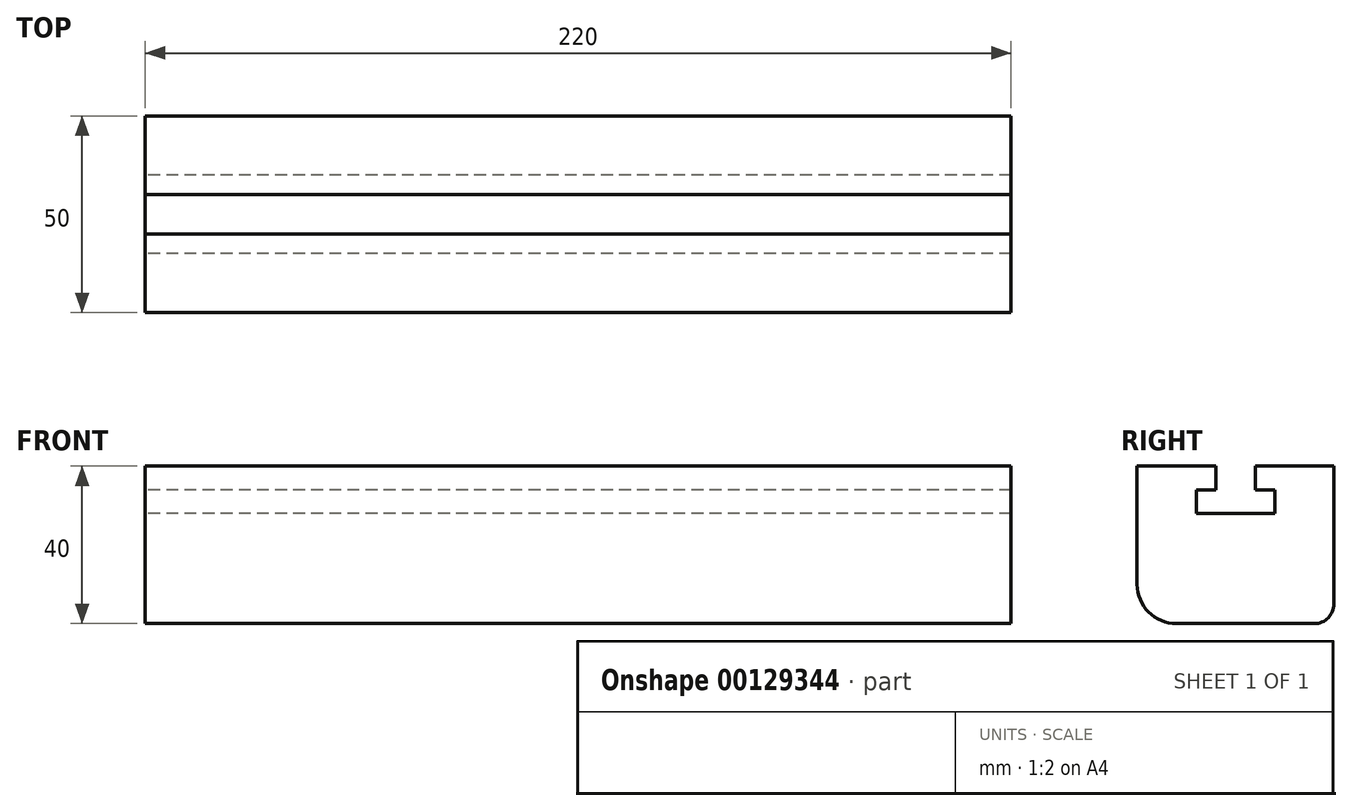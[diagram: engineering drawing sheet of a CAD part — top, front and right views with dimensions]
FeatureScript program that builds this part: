
annotation { "Feature Type Name" : "Feature", "Feature Type Description" : "" }
export const myFeature = defineFeature(function(context is Context, id is Id, definition is map)
    precondition{}
    {
        {
            var Q0;
            Q0=qCreatedBy(makeId("Right.planeOp"),FACE);
            var sketch = newSketch(context, id + "F0", { "sketchPlane" : qUnion([Q0])});
            skLineSegment(sketch, "E0.bottom", {"start": v(50, 40) * mm, "end": v(30, 40) * mm});
            skLineSegment(sketch, "E0.top", {"start": v(45, 0) * mm, "end": v(0, 0) * mm});
            skLineSegment(sketch, "E0.left", {"start": v(50, 40) * mm, "end": v(50, 5) * mm});
            skLineSegment(sketch, "E0.right", {"start": v(0, 40) * mm, "end": v(0, 0) * mm});
            skPoint(sketch, "E1.visualSharp", {"position": v(50, 0) * mm});
            skArc(sketch, "E1.filletArc", {"start": v(45, 0) * mm, "mid": v(48.54, 1.46) * mm, "end": v(50, 5) * mm});
            skLineSegment(sketch, "E2.left", {"start": v(30, 40) * mm, "end": v(30, 34) * mm});
            skLineSegment(sketch, "E2.right", {"start": v(20, 40) * mm, "end": v(20, 34) * mm});
            skLineSegment(sketch, "E3.bottom", {"start": v(35, 34) * mm, "end": v(30, 34) * mm});
            skLineSegment(sketch, "E3.top", {"start": v(35, 28) * mm, "end": v(15, 28) * mm});
            skLineSegment(sketch, "E3.left", {"start": v(35, 34) * mm, "end": v(35, 28) * mm});
            skLineSegment(sketch, "E3.right", {"start": v(15, 34) * mm, "end": v(15, 28) * mm});
            skPoint(sketch, "E4.orphan", {"position": v(20, 30) * mm});
            skLineSegment(sketch, "E5.trimOffspring", {"start": v(20, 34) * mm, "end": v(15, 34) * mm});
            skPoint(sketch, "E2.bottom.end.orphan", {"position": v(20, 55) * mm});
            skLineSegment(sketch, "E6.trimOffspring", {"start": v(20, 40) * mm, "end": v(0, 40) * mm});
            skSolve(sketch);
        }
        {
            var Q0;
            Q0=makeQuery(id+"F0.imprint","IMPRINT",FACE,{"disambiguationData":[TD([[makeQuery(id+"F0.imprint","IMPRINT",EDGE,{"derivedFrom":sQuery(id+"F0.wireOp",EDGE,"E0.bottom")}),1.0]])]});
            extrude(context, id + "F1", {"entities" : qUnion([Q0]), "depth" : 220 * mm});
        }
        {
            var Q0;
            Q0=makeQuery(id+"F1.opExtrude","SWEPT_EDGE",EDGE,{"disambiguationData":[OSD([sQuery(id+"F0.wireOp",EDGE,"E0.top"),sQuery(id+"F0.wireOp",EDGE,"E0.right")])]});
            fillet(context, id + "F2", {"entities" : qUnion([Q0]), "radius" : 10 * mm, "tangentPropagation" : true, "allowEdgeOverflow" : false});
        }
    });
